FCSTD DOCUMENT  (FreeCAD 1.0R39319 (Git))
Label: sketch4
License: All rights reserved
LicenseURL: https://en.wikipedia.org/wiki/All_rights_reserved
objects: Sketcher::SketchObject×1, PartDesign::Body×1
note: 3 computed .brp shape members not serialized (recipe doc carries the construction recipe); baked Part::Feature solids carry a one-line shape summary decoded from their .brp

FEATURE [Sketcher::SketchObject] Sketch
  ArcFitTolerance = 1e-06
  AttachmentSupport = -> [XY_Plane]
  FullyConstrained = true
  MakeInternals = false
  MapMode = 5
  sketch-geometry (27):
    g0: Circle CenterX=0 CenterY=0 CenterZ=0 NormalX=0 NormalY=0 NormalZ=1 AngleXU=0 Radius=44
    g1: ArcOfCircle CenterX=-113 CenterY=0 CenterZ=0 NormalX=0 NormalY=0 NormalZ=1 AngleXU=0 Radius=26 StartAngle=0.418591 EndAngle=5.91196
    g2: ArcOfCircle CenterX=113 CenterY=0 CenterZ=0 NormalX=0 NormalY=0 NormalZ=1 AngleXU=0 Radius=26 StartAngle=3.51282 EndAngle=9.00619
    g3: ArcOfCircle CenterX=0 CenterY=113 CenterZ=0 NormalX=0 NormalY=0 NormalZ=1 AngleXU=0 Radius=26 StartAngle=5.15587 EndAngle=10.6485
    g4: ArcOfCircle CenterX=0 CenterY=-113 CenterZ=0 NormalX=0 NormalY=0 NormalZ=1 AngleXU=0 Radius=26 StartAngle=1.91787 EndAngle=7.4105
    g5: ArcOfCircle CenterX=-85.0841 CenterY=-59.8055 CenterZ=0 NormalX=0 NormalY=0 NormalZ=1 AngleXU=0 Radius=40 StartAngle=0.612669 EndAngle=2.00752
    g6: ArcOfCircle CenterX=0 CenterY=0 CenterZ=0 NormalX=0 NormalY=0 NormalZ=1 AngleXU=0 Radius=64 StartAngle=3.75426 EndAngle=4.10362
    g7: ArcOfCircle CenterX=-59.4734 CenterY=-85.3166 CenterZ=0 NormalX=0 NormalY=0 NormalZ=1 AngleXU=0 Radius=40 StartAngle=5.93618 EndAngle=7.24521
    g8: ArcOfCircle CenterX=85.7124 CenterY=-59.999 CenterZ=0 NormalX=0 NormalY=0 NormalZ=1 AngleXU=0 Radius=40 StartAngle=1.1854 EndAngle=2.53086
    g9: ArcOfCircle CenterX=0 CenterY=0 CenterZ=0 NormalX=0 NormalY=0 NormalZ=1 AngleXU=0 Radius=64.6255 StartAngle=5.31787 EndAngle=5.67246
    g10: ArcOfCircle CenterX=59.5486 CenterY=-86.026 CenterZ=0 NormalX=0 NormalY=0 NormalZ=1 AngleXU=0 Radius=40 StartAngle=2.17628 EndAngle=3.47136
    g11: Circle CenterX=0 CenterY=0 CenterZ=0 NormalX=0 NormalY=0 NormalZ=1 AngleXU=0 Radius=55
    g12: Circle CenterX=-113 CenterY=0 CenterZ=0 NormalX=0 NormalY=0 NormalZ=1 AngleXU=0 Radius=20
    g13: Circle CenterX=0 CenterY=113 CenterZ=0 NormalX=0 NormalY=0 NormalZ=1 AngleXU=0 Radius=20
    g14: Circle CenterX=113 CenterY=0 CenterZ=0 NormalX=0 NormalY=0 NormalZ=1 AngleXU=0 Radius=20
    g15: Circle CenterX=0 CenterY=-113 CenterZ=0 NormalX=0 NormalY=0 NormalZ=1 AngleXU=0 Radius=20
    g16: LineSegment StartX=-18.3848 StartY=131.385 StartZ=0 EndX=-131.385 EndY=18.3848 EndZ=0
    g17: LineSegment StartX=18.3848 StartY=131.385 StartZ=0 EndX=131.385 EndY=18.3848 EndZ=0
    g18: Circle [constr] CenterX=0 CenterY=0 CenterZ=0 NormalX=0 NormalY=0 NormalZ=1 AngleXU=0 Radius=113
    g19: LineSegment StartX=-96.0203 StartY=10.5683 StartZ=0 EndX=-42.7119 EndY=10.5683 EndZ=0
    g20: LineSegment StartX=-95.3636 StartY=-9.43168 StartZ=0 EndX=-42.9772 EndY=-9.43168 EndZ=0
    g21: LineSegment StartX=-8.84381 StartY=95.0616 StartZ=0 EndX=-8.84381 EndY=43.1021 EndZ=0
    g22: LineSegment StartX=11.1562 StartY=96.4006 StartZ=0 EndX=11.1562 EndY=42.5622 EndZ=0
    g23: LineSegment StartX=96.0203 StartY=10.5683 StartZ=0 EndX=42.7119 EndY=10.5683 EndZ=0
    g24: LineSegment StartX=95.3636 StartY=-9.43168 StartZ=0 EndX=42.9772 EndY=-9.43168 EndZ=0
    g25: LineSegment StartX=-8.84381 StartY=-95.0616 StartZ=0 EndX=-8.84381 EndY=-43.1021 EndZ=0
    g26: LineSegment StartX=11.1562 StartY=-96.4006 StartZ=0 EndX=11.1562 EndY=-42.5622 EndZ=0
  constraints (86):
    c: Coincident(g0,g-1)
    c: PointOnObject(g1,g-1)
    c: PointOnObject(g2,g-1)
    c: PointOnObject(g3,g-2)
    c: PointOnObject(g4,g-2)
    c: Diameter(g0) = 88
    c: Diameter(g1) = 52
    c: Equal(g1,g3)
    c: Equal(g3,g2)
    c: Equal(g2,g4)
    c: DistanceX(g1,g0) = 113
    c: Tangent(g5,g6) = 1.5708
    c: Tangent(g6,g7) = 1.5708
    c: PointOnObject(g7,g4)
    c: Coincident(g0,g6)
    c: PointOnObject(g5,g1)
    c: Radius(g5) = 40
    c: Radius(g6) = 64
    c: Radius(g7) = 40
    c: DistanceY(g-1,g3) = 113
    c: DistanceY(g4,g0) = 113
    c: Tangent(g8,g9) = 1.5708
    c: Tangent(g9,g10) = 1.5708
    c: Radius(g8) = 40
    c: Radius(g10) = 40
    c: PointOnObject(g8,g2)
    c: Coincident(g9,g0)
    c: DistanceX(g-1,g2) = 113
    c: Block(g8)
    c: Block(g9)
    c: Block(g10)
    c: Block(g5)
    c: Block(g6)
    c: Block(g7)
    c: Diameter(g11) = 110
    c: Coincident(g11,g0)
    c: Coincident(g12,g1)
    c: Coincident(g13,g3)
    c: Coincident(g14,g2)
    c: Coincident(g15,g4)
    c: Diameter(g12) = 40
    c: Equal(g12,g13)
    c: Equal(g13,g14)
    c: Equal(g14,g15)
    c: Tangent(g17,g3) = 1.5708
    c: Tangent(g17,g2) = 1.5708
    c: Tangent(g16,g1) = -1.5708
    c: Tangent(g16,g3) = -1.5708
    c: Coincident(g18,g0)
    c: PointOnObject(g2,g18)
    c: PointOnObject(g19,g12)
    c: PointOnObject(g19,g0)
    c: Horizontal(g19)
    c: PointOnObject(g20,g12)
    c: PointOnObject(g20,g0)
    c: Horizontal(g20)
    c: PointOnObject(g21,g13)
    c: PointOnObject(g21,g0)
    c: Vertical(g21)
    c: PointOnObject(g22,g13)
    c: PointOnObject(g22,g0)
    c: Vertical(g22)
    c: Distance(g20,g19) = 20
    c: Distance(g22,g21) = 20
    c: PointOnObject(g1,g20)
    c: PointOnObject(g1,g19)
    c: PointOnObject(g3,g21)
    c: PointOnObject(g3,g22)
    c: Horizontal(g23)
    c: Horizontal(g24)
    c: Distance(g24,g23) = 20
    c: Vertical(g25)
    c: Vertical(g26)
    c: Distance(g26,g25) = 20
    c: PointOnObject(g2,g23)
    c: PointOnObject(g2,g24)
    c: PointOnObject(g4,g26)
    c: PointOnObject(g4,g25)
    c: Block(g19)
    c: Block(g20)
    c: Block(g21)
    c: Block(g22)
    c: Block(g23)
    c: Block(g24)
    c: Block(g26)
    c: Block(g25)
FEATURE [PartDesign::Body] Body
  AllowCompound = false
  Group = -> [Sketch]
  Origin = -> Origin
